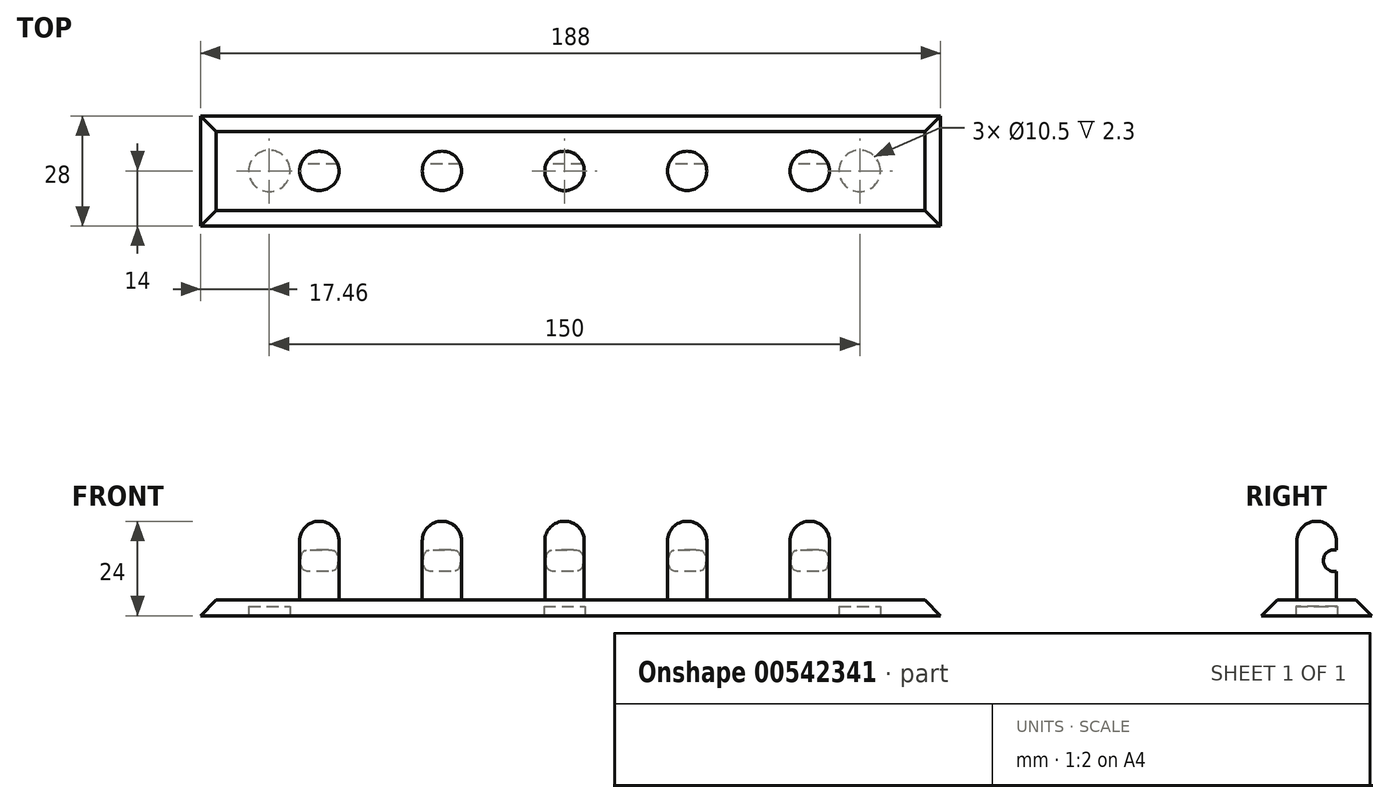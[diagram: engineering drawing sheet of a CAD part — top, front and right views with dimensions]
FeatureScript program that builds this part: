
annotation { "Feature Type Name" : "Feature", "Feature Type Description" : "" }
export const myFeature = defineFeature(function(context is Context, id is Id, definition is map)
    precondition{}
    {
        {
            var Q0;
            Q0=qCreatedBy(makeId("Top.planeOp"),FACE);
            var sketch = newSketch(context, id + "F0", { "sketchPlane" : qUnion([Q0])});
            skLineSegment(sketch, "E0.bottom", {"start": v(-93.46, 15) * mm, "end": v(96.54, 15) * mm});
            skLineSegment(sketch, "E0.top", {"start": v(-93.46, -15) * mm, "end": v(96.54, -15) * mm});
            skLineSegment(sketch, "E0.left", {"start": v(-93.46, 15) * mm, "end": v(-93.46, -15) * mm});
            skLineSegment(sketch, "E0.right", {"start": v(96.54, 15) * mm, "end": v(96.54, -15) * mm});
            skSolve(sketch);
        }
        {
            var Q0;
            Q0 = qSketchRegion(id + "F0", true);
            extrude(context, id + "F1", {"entities" : qUnion([Q0]), "depth" : -4 * mm, "offsetDistance" : 25 * mm});
        }
        {
            var Q0;
            Q0=qCreatedBy(makeId("Top.planeOp"),FACE);
            var sketch = newSketch(context, id + "F2", { "sketchPlane" : qUnion([Q0])});
            skCircle(sketch, "E1", {"center": v(-62.3, 0) * mm, "radius": 5 * mm});
            skCircle(sketch, "E2.1.0.0", {"center": v(-31.15, 0) * mm, "radius": 5 * mm});
            skCircle(sketch, "E2.2.0.0", {"center": v(0, 0) * mm, "radius": 5 * mm});
            skCircle(sketch, "E2.3.0.0", {"center": v(31.15, 0) * mm, "radius": 5 * mm});
            skCircle(sketch, "E2.4.0.0", {"center": v(62.3, 0) * mm, "radius": 5 * mm});
            skLineSegment(sketch, "E2.direction1", {"start": v(-62.3, 0) * mm, "end": v(-31.15, 0) * mm, "construction": true});
            skSolve(sketch);
        }
        {
            var Q0;
            Q0 = qSketchRegion(id + "F2", true);
            extrude(context, id + "F3", {"entities" : qUnion([Q0]), "operationType" : NewBodyOperationType.ADD, "depth" : 20 * mm, "offsetDistance" : 25 * mm});
        }
        {
            var Q0;
            Q0=makeQuery(id+"F1.opExtrude","CAP_FACE",FACE,{"disambiguationData":[OSD([sQuery(id+"F0.wireOp",EDGE,"E0.bottom"),sQuery(id+"F0.wireOp",EDGE,"E0.top"),sQuery(id+"F0.wireOp",EDGE,"E0.left"),sQuery(id+"F0.wireOp",EDGE,"E0.right")])],"isStart":false});
            var sketch = newSketch(context, id + "F4", { "sketchPlane" : qUnion([Q0])});
            skCircle(sketch, "E3", {"center": v(-75, 0) * mm, "radius": 5.25 * mm});
            skCircle(sketch, "E4.1.0.0", {"center": v(0, 0) * mm, "radius": 5.25 * mm});
            skCircle(sketch, "E4.2.0.0", {"center": v(75, 0) * mm, "radius": 5.25 * mm});
            skLineSegment(sketch, "E4.direction1", {"start": v(-75, 0) * mm, "end": v(0, 0) * mm, "construction": true});
            skSolve(sketch);
        }
        {
            var Q0;
            Q0 = qSketchRegion(id + "F4", true);
            extrude(context, id + "F5", {"entities" : qUnion([Q0]), "operationType" : NewBodyOperationType.REMOVE, "oppositeDirection" : true, "depth" : 2.3 * mm, "offsetDistance" : 25 * mm});
        }
        {
            var Q0;
            Q0=makeQuery(id+"F1.opExtrude","CAP_EDGE",EDGE,{"disambiguationData":[OSD([sQuery(id+"F0.wireOp",EDGE,"E0.bottom")])],"isStart":true});
            var Q1;
            Q1=makeQuery(id+"F1.opExtrude","CAP_EDGE",EDGE,{"disambiguationData":[OSD([sQuery(id+"F0.wireOp",EDGE,"E0.top")])],"isStart":true});
            var Q2;
            Q2=makeQuery(id+"F1.opExtrude","CAP_EDGE",EDGE,{"disambiguationData":[OSD([sQuery(id+"F0.wireOp",EDGE,"E0.right")])],"isStart":true});
            var Q3;
            Q3=makeQuery(id+"F1.opExtrude","CAP_EDGE",EDGE,{"disambiguationData":[OSD([sQuery(id+"F0.wireOp",EDGE,"E0.left")])],"isStart":true});
            chamfer(context, id + "F6", {"entities" : qUnion([Q0, Q1, Q2, Q3]), "width" : 5 * mm, "tangentPropagation" : true});
        }
        {
            var Q0;
            Q0=qCreatedBy(makeId("Right.planeOp"),FACE);
            var sketch = newSketch(context, id + "F7", { "sketchPlane" : qUnion([Q0])});
            skCircle(sketch, "E5", {"center": v(4.44, 10) * mm, "radius": 2.75 * mm});
            skSolve(sketch);
        }
        {
            var Q0;
            Q0 = qSketchRegion(id + "F7", true);
            extrude(context, id + "F8", {"entities" : qUnion([Q0]), "operationType" : NewBodyOperationType.REMOVE, "endBound" : BoundingType.SYMMETRIC, "depth" : 150 * mm, "offsetDistance" : 25 * mm});
        }
        {
            var Q0;
            Q0=makeQuery(id+"F3.opExtrude","CAP_EDGE",EDGE,{"disambiguationData":[OSD([sQuery(id+"F2.wireOp",EDGE,"E1")])],"isStart":false});
            var Q1;
            Q1=makeQuery(id+"F3.opExtrude","CAP_FACE",FACE,{"disambiguationData":[OSD([sQuery(id+"F2.wireOp",EDGE,"E2.1.0.0")])],"isStart":false});
            var Q2;
            Q2=makeQuery(id+"F3.opExtrude","CAP_EDGE",EDGE,{"disambiguationData":[OSD([sQuery(id+"F2.wireOp",EDGE,"E2.2.0.0")])],"isStart":false});
            var Q3;
            Q3=makeQuery(id+"F3.opExtrude","CAP_EDGE",EDGE,{"disambiguationData":[OSD([sQuery(id+"F2.wireOp",EDGE,"E2.3.0.0")])],"isStart":false});
            var Q4;
            Q4=makeQuery(id+"F3.opExtrude","CAP_EDGE",EDGE,{"disambiguationData":[OSD([sQuery(id+"F2.wireOp",EDGE,"E2.4.0.0")])],"isStart":false});
            fillet(context, id + "F9", {"entities" : qUnion([Q0, Q1, Q2, Q3, Q4]), "radius" : 5 * mm, "tangentPropagation" : true, "allowEdgeOverflow" : false});
        }
    });
